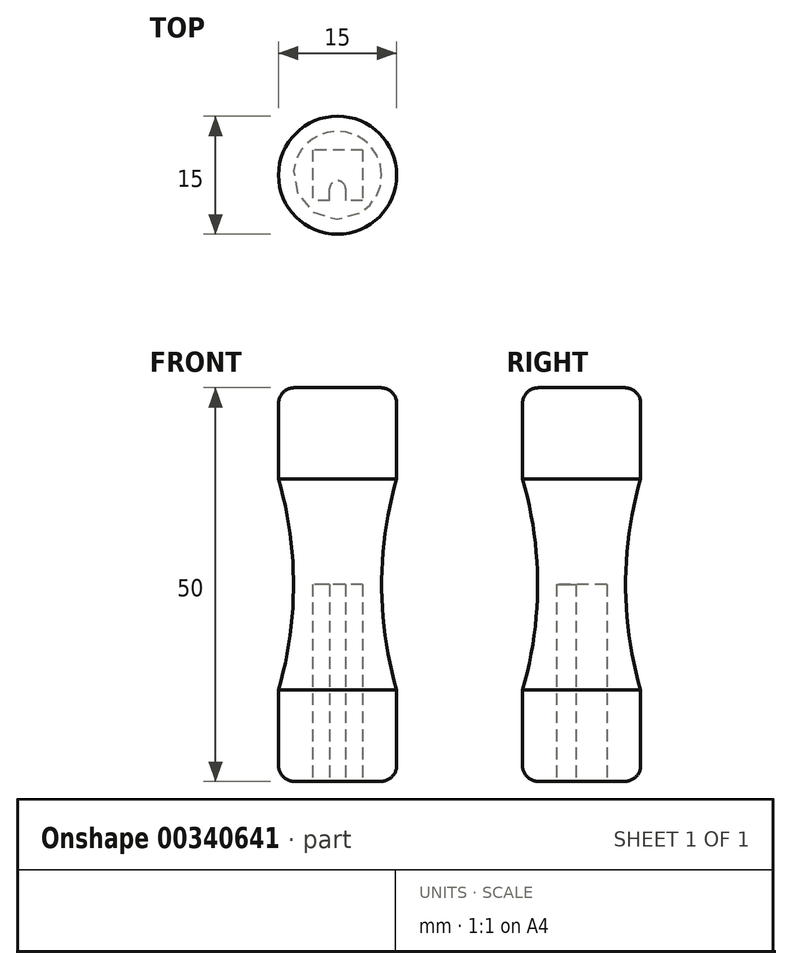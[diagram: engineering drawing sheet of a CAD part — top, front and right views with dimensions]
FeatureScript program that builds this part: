
annotation { "Feature Type Name" : "Feature", "Feature Type Description" : "" }
export const myFeature = defineFeature(function(context is Context, id is Id, definition is map)
    precondition{}
    {
        {
            var Q0;
            Q0=qCreatedBy(makeId("Top.planeOp"),FACE);
            var sketch = newSketch(context, id + "F0", { "sketchPlane" : qUnion([Q0])});
            skCircle(sketch, "E0", {"center": v(0, 0) * mm, "radius": 7.5 * mm});
            skSolve(sketch);
        }
        {
            var Q0;
            Q0 = qSketchRegion(id + "F0", true);
            extrude(context, id + "F1", {"entities" : qUnion([Q0]), "depth" : 50 * mm});
        }
        {
            var Q0;
            Q0=qCreatedBy(makeId("Top.planeOp"),FACE);
            var sketch = newSketch(context, id + "F2", { "sketchPlane" : qUnion([Q0])});
            skLineSegment(sketch, "E1.bottom", {"start": v(3.2, 3.2) * mm, "end": v(-3.2, 3.2) * mm});
            skLineSegment(sketch, "E1.top", {"start": v(3.2, -3.2) * mm, "end": v(1, -3.2) * mm});
            skLineSegment(sketch, "E1.left", {"start": v(3.2, 3.2) * mm, "end": v(3.2, -3.2) * mm});
            skLineSegment(sketch, "E1.right", {"start": v(-3.2, 3.2) * mm, "end": v(-3.2, -3.2) * mm});
            skPoint(sketch, "E1.middle", {"position": v(0, 0) * mm});
            skLineSegment(sketch, "E2", {"start": v(-1, -3.2) * mm, "end": v(-1, -1.7) * mm});
            skLineSegment(sketch, "E3", {"start": v(-1, -1.7) * mm, "end": v(1, -1.7) * mm, "construction": true});
            skLineSegment(sketch, "E4", {"start": v(1, -1.7) * mm, "end": v(1, -3.2) * mm});
            skLineSegment(sketch, "E5", {"start": v(0, -1.7) * mm, "end": v(0, 0) * mm, "construction": true});
            skLineSegment(sketch, "E6", {"start": v(-1, -3.2) * mm, "end": v(-3.2, -3.2) * mm});
            skLineSegment(sketch, "E7", {"start": v(1, -3.2) * mm, "end": v(-1, -3.2) * mm, "construction": true});
            skArc(sketch, "E8", {"start": v(1, -1.7) * mm, "mid": v(0, -0.7) * mm, "end": v(-1, -1.7) * mm});
            skSolve(sketch);
        }
        {
            var Q0;
            Q0 = qSketchRegion(id + "F2", true);
            extrude(context, id + "F3", {"entities" : qUnion([Q0]), "operationType" : NewBodyOperationType.REMOVE, "depth" : 25 * mm});
        }
        {
            var Q0;
            Q0=qCreatedBy(makeId("Front.planeOp"),FACE);
            var sketch = newSketch(context, id + "F4", { "sketchPlane" : qUnion([Q0])});
            skLineSegment(sketch, "E9", {"start": v(-8, 40) * mm, "end": v(-13, 40) * mm});
            skLineSegment(sketch, "E10", {"start": v(-13, 40) * mm, "end": v(-13, 10) * mm});
            skLineSegment(sketch, "E11", {"start": v(-13, 10) * mm, "end": v(-8, 10) * mm});
            skLineSegment(sketch, "E12", {"start": v(-8, 10) * mm, "end": v(-8, 40) * mm, "construction": true});
            skArc(sketch, "E13", {"start": v(-8, 10) * mm, "mid": v(-5.6, 25) * mm, "end": v(-8, 40) * mm});
            skSolve(sketch);
        }
        {
            var Q0;
            Q0 = qSketchRegion(id + "F4", true);
            var Q1;
            Q1=makeQuery(id+"F1.opExtrude","CAP_EDGE",EDGE,{"disambiguationData":[OSD([sQuery(id+"F0.wireOp",EDGE,"E0")])],"isStart":false});
            revolve(context, id + "F5", {"operationType" : NewBodyOperationType.REMOVE, "entities" : qUnion([Q0]), "axis" : qUnion([Q1]), "revolveType" : RevolveType.FULL, "oppositeDirection" : true});
        }
        {
            var Q0;
            Q0=makeQuery(id+"F1.opExtrude","CAP_EDGE",EDGE,{"disambiguationData":[OSD([sQuery(id+"F0.wireOp",EDGE,"E0")])],"isStart":false});
            var Q1;
            Q1=makeQuery(id+"F1.opExtrude","CAP_EDGE",EDGE,{"disambiguationData":[OSD([sQuery(id+"F0.wireOp",EDGE,"E0")])],"isStart":true});
            fillet(context, id + "F6", {"entities" : qUnion([Q0, Q1]), "radius" : 2 * mm, "tangentPropagation" : true, "allowEdgeOverflow" : false});
        }
    });
